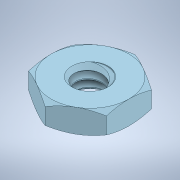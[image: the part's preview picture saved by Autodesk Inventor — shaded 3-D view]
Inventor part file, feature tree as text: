
AUTODESK INVENTOR PART (.ipt)
format: ipt  version: 2021 (Build 250183000, 183)  size: 260,096 bytes
history: native  units: in
note: dims shown in document units (in); Inventor stores cm internally (conversion verified against a paired STEP export)
features: mirror x1
ambient origin geometry x8: Origin, YZ Plane, XZ Plane, XY Plane, X Axis, Y Axis, Z Axis, Center Point
bodies: Solid1 (feature_tree)
feature tree (1):
  mirror  "Mirror1"
